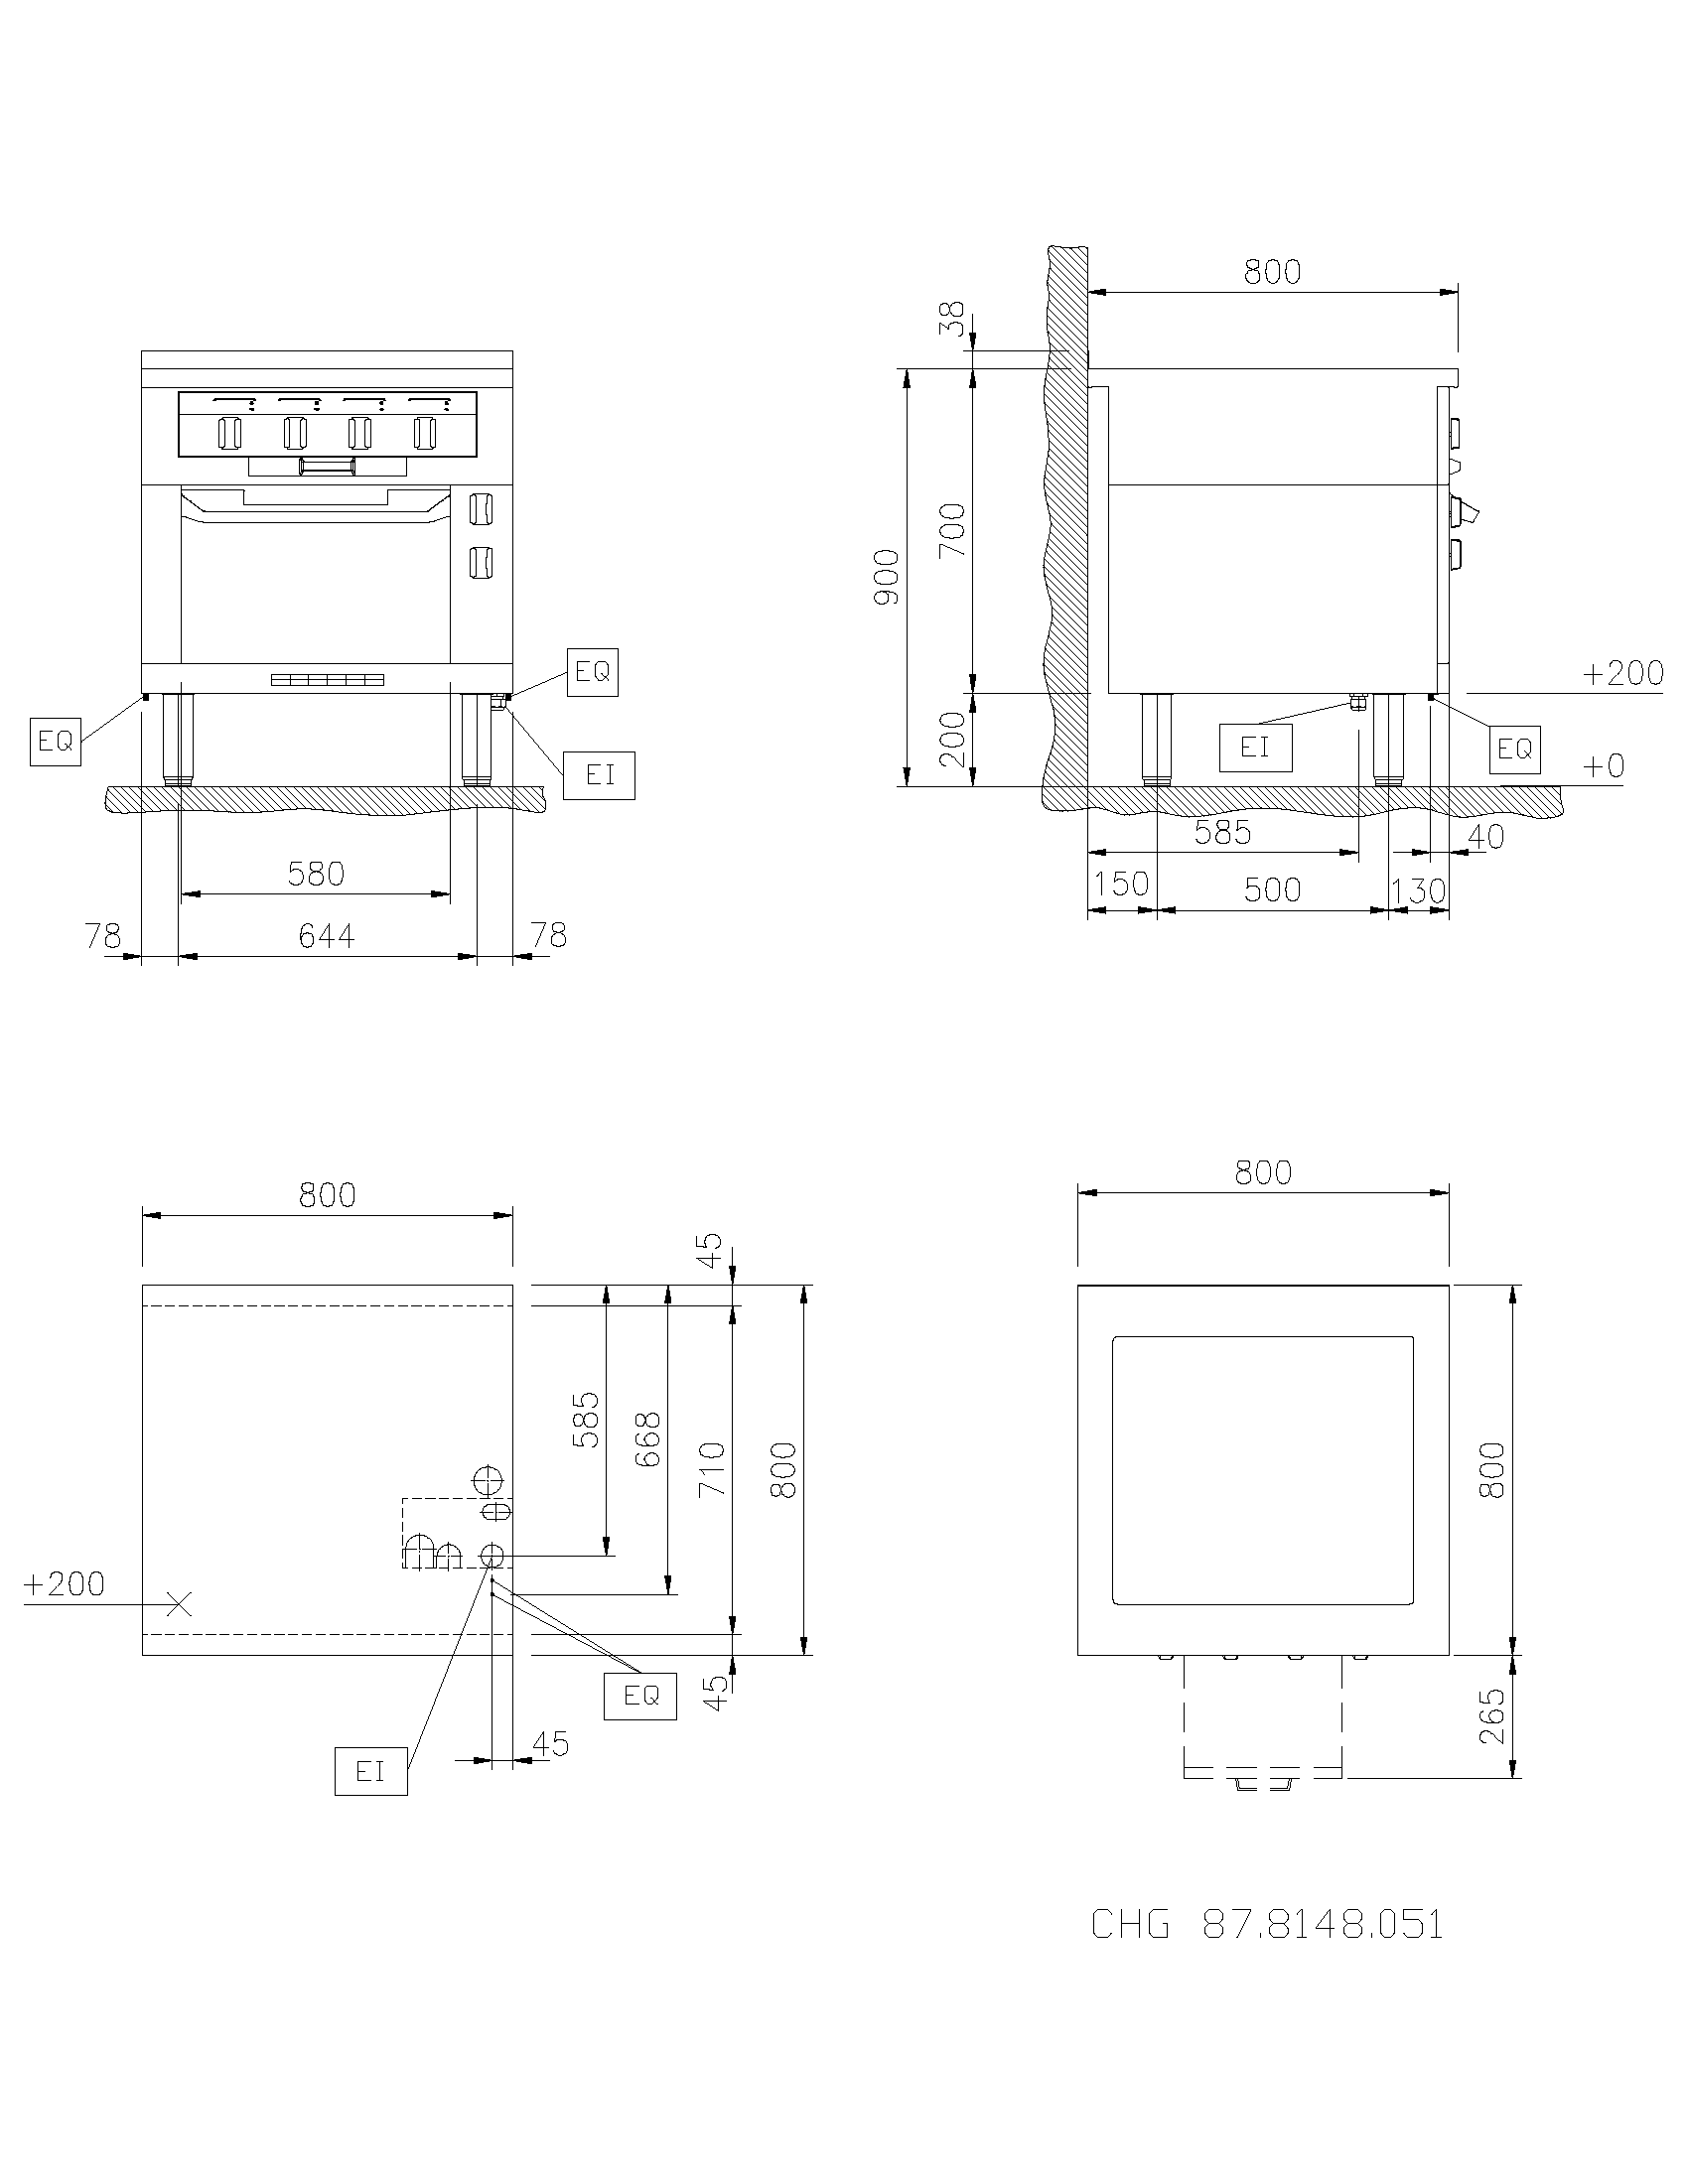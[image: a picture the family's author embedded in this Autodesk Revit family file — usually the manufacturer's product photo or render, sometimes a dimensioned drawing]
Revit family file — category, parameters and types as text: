
# Revit family: QF_ELECTROLUXPROFESSIONAL_589936_HCDFBBKODM
name_source: partatom
category: Specialty Equipment
units: mm (PartAtom-declared; Revit-internal decimal feet)

## family parameters
Always vertical = Yes
Cut with Voids When Loaded = No
Enable Cutting in Views = No
Maintain Annotation Orientation = No
Part Type = Normal
Room Calculation Point = No
Round Connector Dimension = Use Diameter
Shared = No
Work Plane-Based = No

## types (1)
- QF_ELECTROLUXPROFESSIONAL_589936_HCDFBBKODM
    Accessory = No
    Cold Water Size = 1"
    Cycle = 60 Hz
    Default Elevation = 0 mm  [stored 0 ft]
    Depth Actual = 900 mm  [stored 2.95276 ft]
    Description = ELECTRIC CHARGRILL TOP, 1-SIDE, SPLASHBACK, 1200X900X250H MARINE USPHS (ONLY M2M)
    Gas KW = 0
    HP = 21.7 HP
    Height Actual = 250 mm  [stored 0.82021 ft]
    Length Actual = 1200 mm  [stored 3.93701 ft]
    Manufacturer = Electrolux Professional
    Model = HCDFBBKODM
    Phase = 3
    URL = http://www.electroluxprofessional.com
    URL Manufacturer = http://www.electroluxprofessional.com
    Volts = 440 V
    Watts = 0 W
    Weight = 125.00 kg
    Weight in Pounds = 487.22

note: [stored X ft] marks values corroborated as IEEE doubles in the binary element streams (Revit-internal decimal feet)

## geometry (parser evidence)
native form markers: Blend x20, Sweep x23
no freeform markers — native parametric forms only
